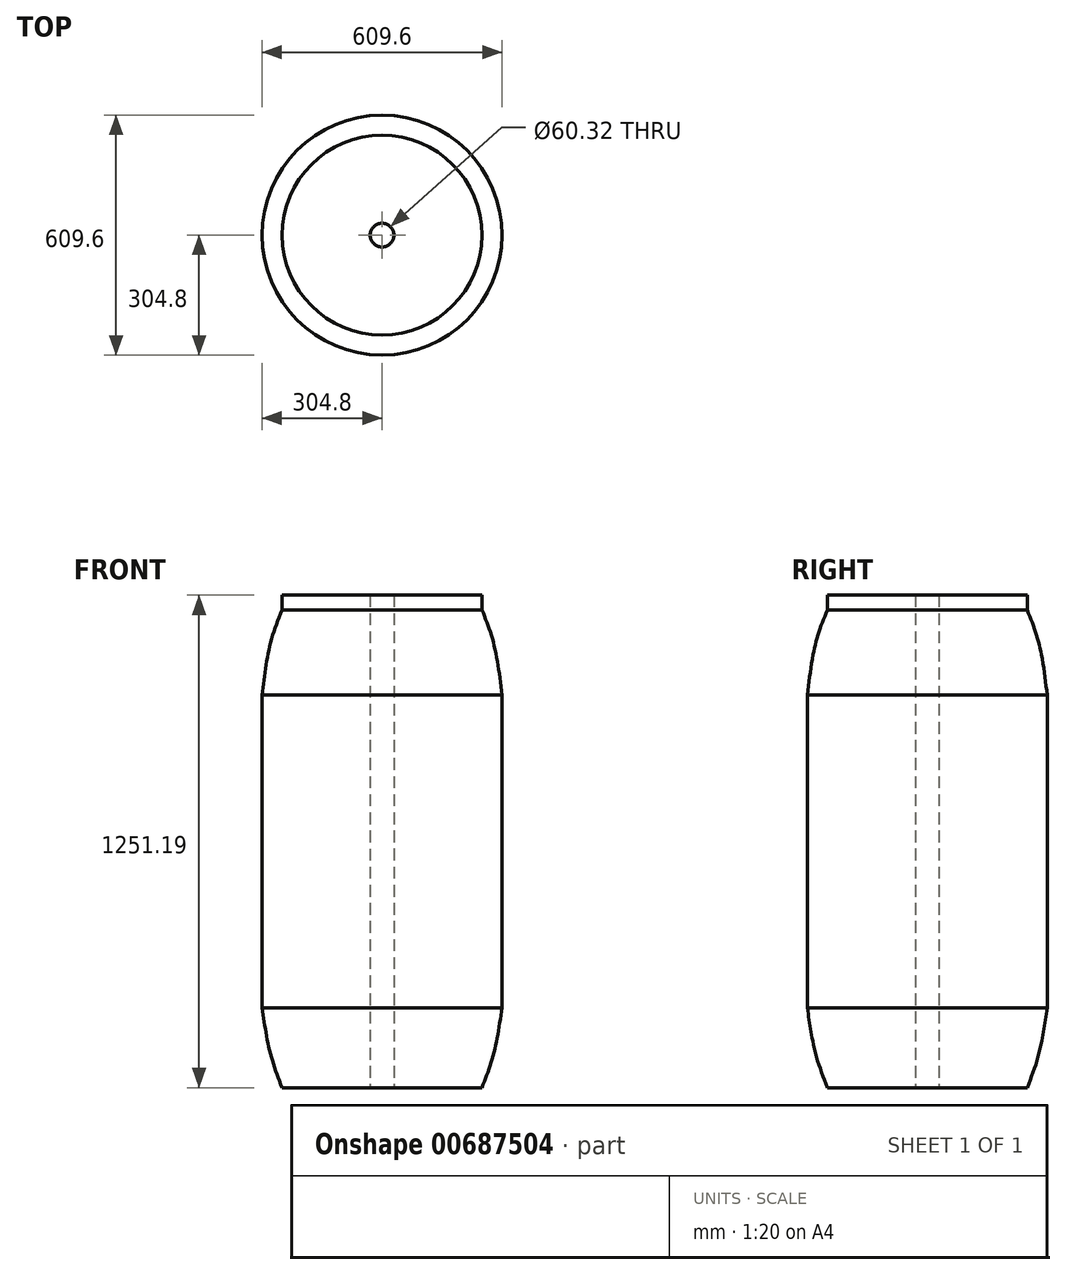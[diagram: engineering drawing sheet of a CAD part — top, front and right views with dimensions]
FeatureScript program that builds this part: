
annotation { "Feature Type Name" : "Feature", "Feature Type Description" : "" }
export const myFeature = defineFeature(function(context is Context, id is Id, definition is map)
    precondition{}
    {
        {
            var Q0;
            Q0=qCreatedBy(makeId("Front.planeOp"),FACE);
            var sketch = newSketch(context, id + "F0", { "sketchPlane" : qUnion([Q0])});
            skLineSegment(sketch, "E0", {"start": v(0, 1251.2) * mm, "end": v(0, 184.4) * mm});
            skLineSegment(sketch, "E1", {"start": v(0, 1251.2) * mm, "end": v(-254, 1251.2) * mm});
            skLineSegment(sketch, "E2", {"start": v(-304.8, 1021.1) * mm, "end": v(-304.8, 203.2) * mm});
            skLineSegment(sketch, "E3", {"start": v(-254, 0) * mm, "end": v(0, 0) * mm});
            skPoint(sketch, "E4", {"position": v(-254, 1251.2) * mm});
            skPoint(sketch, "E5", {"position": v(-304.8, 997.2) * mm});
            skPoint(sketch, "E6", {"position": v(-254, 1213.1) * mm});
            skLineSegment(sketch, "E7", {"start": v(-254, 1251.2) * mm, "end": v(-254, 1213.1) * mm});
            skFitSpline(sketch, "E8", {"points": [v(-254, 1213.1) * mm, v(-283.6, 1128.57) * mm, v(-304.8, 997.2) * mm], "startDerivative": vector(-71.8, -175.93) * mm, "endDerivative": vector(-31.13, -253.32) * mm});
            skLineSegment(sketch, "E9", {"start": v(0, 184.4) * mm, "end": v(0, 0) * mm});
            skPoint(sketch, "E10", {"position": v(-254, 0) * mm});
            skPoint(sketch, "E11", {"position": v(-304.8, 203.2) * mm});
            skFitSpline(sketch, "E12", {"points": [v(-254, 0) * mm, v(-283.98, 87.94) * mm, v(-304.8, 203.2) * mm], "startDerivative": vector(-69.35, 179.32) * mm, "endDerivative": vector(-32.95, 226.18) * mm});
            skPoint(sketch, "E13.orphan", {"position": v(-304.8, 0) * mm});
            skPoint(sketch, "E14.end.orphan", {"position": v(-298.45, 1251.2) * mm});
            skPoint(sketch, "E14.start.orphan", {"position": v(-304.8, 1251.2) * mm});
            skSolve(sketch);
        }
        {
            var Q0;
            Q0=makeQuery(id+"F0.imprint","IMPRINT",FACE,{"disambiguationData":[TD([[makeQuery(id+"F0.imprint","IMPRINT",EDGE,{"derivedFrom":sQuery(id+"F0.wireOp",EDGE,"E0")}),-1.0]])]});
            var Q1;
            Q1=sQuery(id+"F0.wireOp",EDGE,"E0");
            revolve(context, id + "F1", {"entities" : qUnion([Q0]), "axis" : qUnion([Q1]), "revolveType" : RevolveType.FULL});
        }
        {
            var Q0;
            Q0=makeQuery(id+"F1.opRevolve","SWEPT_FACE",FACE,{"disambiguationData":[OSD([sQuery(id+"F0.wireOp",EDGE,"E3")])]});
            var sketch = newSketch(context, id + "F2", { "sketchPlane" : qUnion([Q0])});
            skPoint(sketch, "E15", {"position": v(0, 0) * mm});
            skSolve(sketch);
        }
        {
            var Q0;
            Q0=sQuery(id+"F2.wireOp",VERTEX,"E15");
            var Q1;
            Q1=makeQuery(id+"F1.opRevolve","SWEPT_BODY",BODY,{"disambiguationData":[OSD([sQuery(id+"F0.wireOp",EDGE,"E0"),sQuery(id+"F0.wireOp",EDGE,"E1"),sQuery(id+"F0.wireOp",EDGE,"E2"),sQuery(id+"F0.wireOp",EDGE,"E3"),sQuery(id+"F0.wireOp",EDGE,"E7"),sQuery(id+"F0.wireOp",EDGE,"E8"),sQuery(id+"F0.wireOp",EDGE,"E9"),sQuery(id+"F0.wireOp",EDGE,"E12")])]});
            hole(context, id + "F3", {"style" : HoleStyle.C_BORE, "endStyle" : HoleEndStyle.THROUGH, "holeDiameter" : 60.32 * mm, "cBoreDiameter" : 60.32 * mm, "cBoreDepth" : 4.83 * mm, "majorDiameter" : 6.35 * mm, "isTappedThrough" : true, "tappedDepth" : 12.7 * mm, "tapClearance" : 3, "locations" : qUnion([Q0]), "scope" : qUnion([Q1])});
        }
    });
